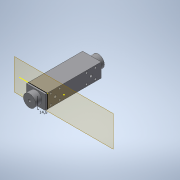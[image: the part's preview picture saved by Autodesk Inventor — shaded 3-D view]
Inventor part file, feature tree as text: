
AUTODESK INVENTOR PART (.ipt)
format: ipt  version: 2020 (Build 240168000, 168)  size: 265,728 bytes
history: native  units: mm
features: extrude x10, sketch x10, reference x9, other x7, projected_geometry x3, hole x1, mirror x1
ambient origin geometry x8: Origin, YZ Plane, XZ Plane, XY Plane, X Axis, Y Axis, Z Axis, Center Point
bodies: Body1 (feature_tree)
feature tree (41):
  other  "Bryła1"
  other  "Płaszczyzna konstrukcyjna1"
  extrude  "Wyciągnięcie proste1"  Depth=3.0mm TaperAngle=0.0deg
  extrude  "Wyciągnięcie proste2"  Depth=6.0mm
  extrude  "Wyciągnięcie proste3"  Depth=20.0mm TaperAngle=0.0deg
  sketch  "Szkic4"
  extrude  "Wyciągnięcie proste4"  Depth=0.25mm
  other  "Płaszczyzna konstrukcyjna2"
  extrude  "Wyciągnięcie proste5"  Depth=0.25mm
  hole  "Otwór3"  [1 undecoded]
  extrude  "Wyciągnięcie proste8"  Depth=0.25mm
  extrude  "Wyciągnięcie proste7"  Depth=20.0mm TaperAngle=0.0deg
  extrude  "Wyciągnięcie proste9"  Depth=14.6mm
  mirror  "Odbij1"
  extrude  "Wyciągnięcie proste10"  TaperAngle=0.0deg  [1 undecoded]
  extrude  "Wyciągnięcie proste11"  Depth=3.0mm TaperAngle=0.0deg
  sketch  "Szkic1"
  reference  "Odniesienie1"
  reference  "Odniesienie2"
  sketch  "Szkic2"
  sketch  "Szkic3"
  reference  "Odniesienie3"
  reference  "Odniesienie4"
  reference  "Odniesienie5"
  reference  "Odniesienie6"
  reference  "Odniesienie7"
  sketch  "Szkic5"
  projected_geometry  "Pętla rzutowana1"
  sketch  "Szkic6"
  sketch  "Szkic7"
  reference  "Odniesienie8"
  reference  "Odniesienie9"
  sketch  "Szkic8"
  projected_geometry  "Pętla rzutowana2"
  sketch  "Szkic9"
  projected_geometry  "Pętla rzutowana3"
  sketch  "Szkic11"
  other  "<userpath>\Desktop\3d\scanning-robot\Assembly1.iam"
  other  "Assembly1.iam"
  other  "wheel-adapter:1"
  other  "wheel:1"
note: 2 required parameter values undecoded (feature->parameter linkage not recoverable at this tier; creation-order binding heuristic only, values carry confidence <= 0.55)
